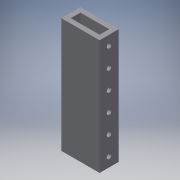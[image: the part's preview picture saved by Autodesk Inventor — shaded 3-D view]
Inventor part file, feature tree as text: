
AUTODESK INVENTOR PART (.ipt)
format: ipt  version: 2017 (Build 210142000, 142)  size: 121,344 bytes
history: native  units: in
note: dims shown in document units (in); Inventor stores cm internally (conversion verified against a paired STEP export)
features: extrude x2, sketch x2
ambient origin geometry x8: Origin, YZ Plane, XZ Plane, XY Plane, X Axis, Y Axis, Z Axis, Center Point
bodies: Solid1 (feature_tree)
feature tree (4):
  extrude  "Extrusion1"  Depth=1.0in
  extrude  "Extrusion2"  Depth=6.0in TaperAngle=0.0deg
  sketch  "Sketch1"  dims[d0=2.0in d1=1.0in]
  sketch  "Sketch2"  dims[d2=0.25in d3=6.0in d4=0.0in d5=0.25in d6=0.5in d7=2.3622in d9=1.0in d10=0.3937in d12=1.0in d14=6.0in d15=0.0in]
